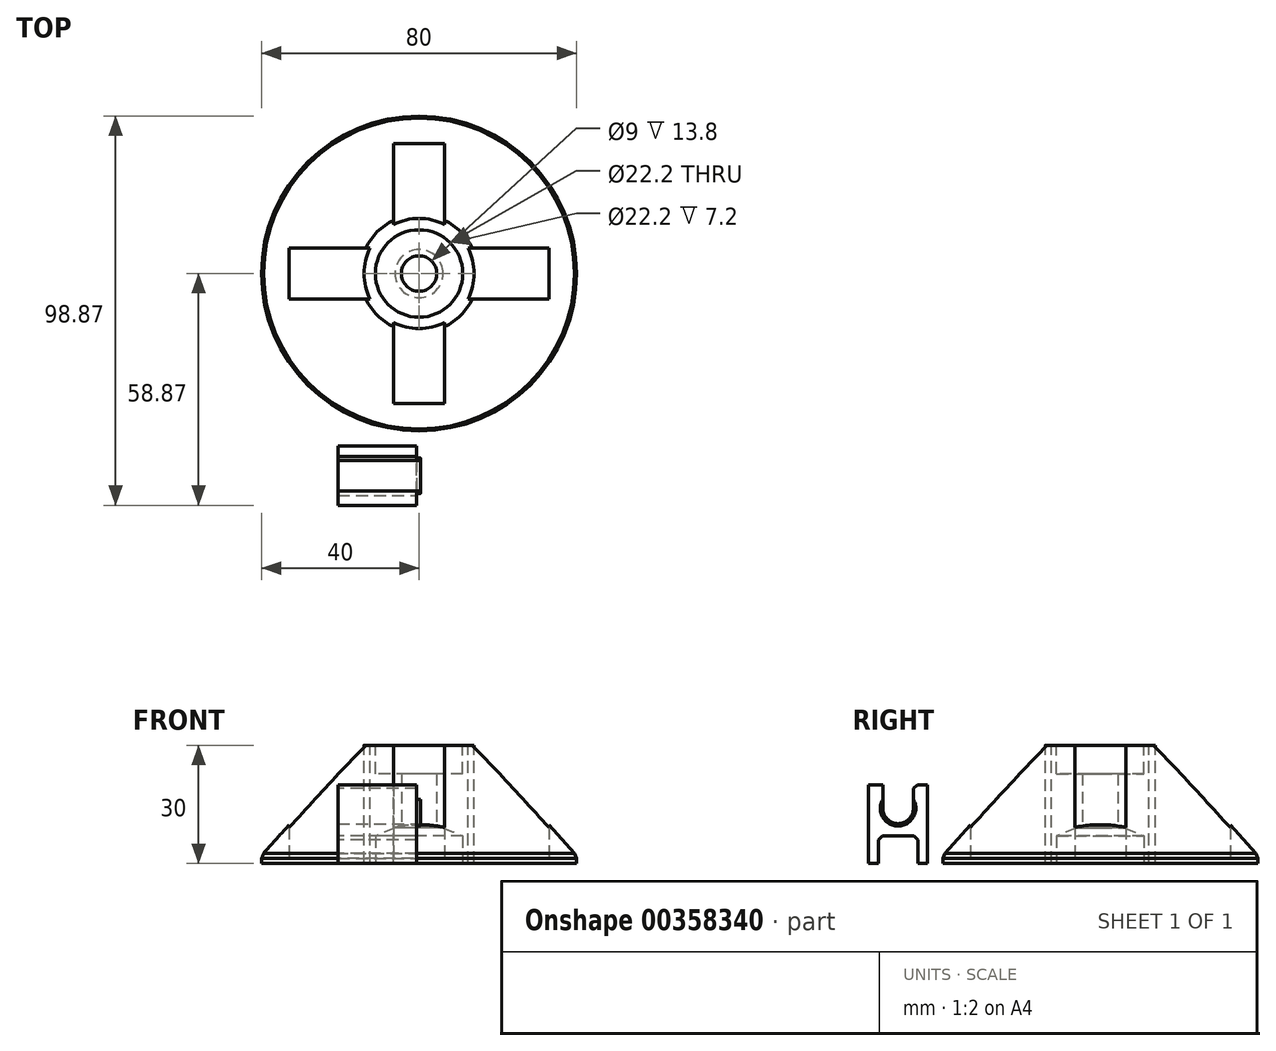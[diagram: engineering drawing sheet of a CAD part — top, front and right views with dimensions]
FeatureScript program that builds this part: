
annotation { "Feature Type Name" : "Feature", "Feature Type Description" : "" }
export const myFeature = defineFeature(function(context is Context, id is Id, definition is map)
    precondition{}
    {
        {
            var Q0;
            Q0=qCreatedBy(makeId("Top.planeOp"),FACE);
            var sketch = newSketch(context, id + "F0", { "sketchPlane" : qUnion([Q0])});
            skCircle(sketch, "E0", {"center": v(0, 0) * mm, "radius": 40 * mm});
            skLineSegment(sketch, "E1.bottom", {"start": v(-6.5, 33) * mm, "end": v(6.5, 33) * mm});
            skLineSegment(sketch, "E1.top", {"start": v(-6.5, 8) * mm, "end": v(6.5, 8) * mm});
            skLineSegment(sketch, "E1.left", {"start": v(-6.5, 33) * mm, "end": v(-6.5, 8) * mm});
            skLineSegment(sketch, "E1.right", {"start": v(6.5, 33) * mm, "end": v(6.5, 8) * mm});
            skPoint(sketch, "E1.middle", {"position": v(0, 20.5) * mm});
            skLineSegment(sketch, "E2", {"start": v(0, 33) * mm, "end": v(0, 40) * mm});
            skCircle(sketch, "E3", {"center": v(0, 0) * mm, "radius": 4.5 * mm});
            skLineSegment(sketch, "E4", {"start": v(0, 20.5) * mm, "end": v(0, 0) * mm});
            skLineSegment(sketch, "E5.bottom", {"start": v(-33, -6.5) * mm, "end": v(-33, 6.5) * mm});
            skLineSegment(sketch, "E5.top", {"start": v(-8, -6.5) * mm, "end": v(-8, 6.5) * mm});
            skLineSegment(sketch, "E5.left", {"start": v(-33, -6.5) * mm, "end": v(-8, -6.5) * mm});
            skLineSegment(sketch, "E5.right", {"start": v(-33, 6.5) * mm, "end": v(-8, 6.5) * mm});
            skPoint(sketch, "E5.middle", {"position": v(-20.5, 0) * mm});
            skLineSegment(sketch, "E6", {"start": v(-20.5, 0) * mm, "end": v(0, 0) * mm});
            skLineSegment(sketch, "E7.bottom", {"start": v(33, 6.5) * mm, "end": v(33, -6.5) * mm});
            skLineSegment(sketch, "E7.top", {"start": v(8, 6.5) * mm, "end": v(8, -6.5) * mm});
            skLineSegment(sketch, "E7.left", {"start": v(33, 6.5) * mm, "end": v(8, 6.5) * mm});
            skLineSegment(sketch, "E7.right", {"start": v(33, -6.5) * mm, "end": v(8, -6.5) * mm});
            skPoint(sketch, "E7.middle", {"position": v(20.5, 0) * mm});
            skLineSegment(sketch, "E8", {"start": v(20.5, 0) * mm, "end": v(0, 0) * mm});
            skLineSegment(sketch, "E9.bottom", {"start": v(6.5, -33) * mm, "end": v(-6.5, -33) * mm});
            skLineSegment(sketch, "E9.top", {"start": v(6.5, -8) * mm, "end": v(-6.5, -8) * mm});
            skLineSegment(sketch, "E9.left", {"start": v(6.5, -33) * mm, "end": v(6.5, -8) * mm});
            skLineSegment(sketch, "E9.right", {"start": v(-6.5, -33) * mm, "end": v(-6.5, -8) * mm});
            skPoint(sketch, "E9.middle", {"position": v(0, -20.5) * mm});
            skLineSegment(sketch, "E10", {"start": v(0, -20.5) * mm, "end": v(0, 0) * mm});
            skSolve(sketch);
        }
        {
            var Q0;
            Q0=qCreatedBy(makeId("Top.planeOp"),FACE);
            cPlane(context, id + "F1", {"entities" : qUnion([Q0]), "cplaneType" : CPlaneType.OFFSET, "offset" : 2 * mm, "width" : 150 * mm, "height" : 150 * mm});
        }
        {
            var Q0;
            Q0=qCreatedBy(id+"F1.planeOp",FACE);
            var sketch = newSketch(context, id + "F2", { "sketchPlane" : qUnion([Q0])});
            skCircle(sketch, "E11", {"center": v(0, 0) * mm, "radius": 40 * mm});
            skSolve(sketch);
        }
        {
            var Q0;
            Q0=qCreatedBy(makeId("Top.planeOp"),FACE);
            cPlane(context, id + "F3", {"entities" : qUnion([Q0]), "cplaneType" : CPlaneType.OFFSET, "offset" : 30 * mm, "width" : 150 * mm, "height" : 150 * mm});
        }
        {
            var Q0;
            Q0=qCreatedBy(id+"F3.planeOp",FACE);
            var sketch = newSketch(context, id + "F4", { "sketchPlane" : qUnion([Q0])});
            skCircle(sketch, "E12", {"center": v(0, 0) * mm, "radius": 15 * mm});
            skSolve(sketch);
        }
        {
            var Q0;
            Q0=makeQuery(id+"F2.imprint","IMPRINT",FACE,{"disambiguationData":[TD([[makeQuery(id+"F2.imprint","IMPRINT",EDGE,{"derivedFrom":sQuery(id+"F2.wireOp",EDGE,"E11")}),1.0]])]});
            var Q1;
            Q1=makeQuery(id+"F4.imprint","IMPRINT",FACE,{"disambiguationData":[TD([[makeQuery(id+"F4.imprint","IMPRINT",EDGE,{"derivedFrom":sQuery(id+"F4.wireOp",EDGE,"E12")}),1.0]])]});
            loft(context, id + "F5", {"sheetProfilesArray" : [{ "sheetProfileEntities" : qUnion([Q0]) }, { "sheetProfileEntities" : qUnion([Q1]) }]});
        }
        {
            var Q0;
            Q0=makeQuery(id+"F0.imprint","IMPRINT",FACE,{"disambiguationData":[TD([[makeQuery(id+"F0.imprint","IMPRINT",EDGE,{"derivedFrom":sQuery(id+"F0.wireOp",EDGE,"E0")}),1.0]])]});
            extrude(context, id + "F6", {"entities" : qUnion([Q0]), "operationType" : NewBodyOperationType.ADD, "depth" : 2 * mm});
        }
        {
            var Q0;
            Q0=makeQuery(id+"F6.boolean.opBoolean","SPLIT",FACE,{"disambiguationData":[TD([makeQuery(id+"F6.opExtrude","SWEPT_FACE",FACE,{"disambiguationData":[OSD([sQuery(id+"F0.wireOp",EDGE,"E5.bottom")])]})])],"derivedFrom":makeQuery(id+"F5.opLoft","CAP_FACE",FACE,{"disambiguationData":[OSD([makeQuery(id+"F2.imprint","IMPRINT",FACE,{"disambiguationData":[TD([[makeQuery(id+"F2.imprint","IMPRINT",EDGE,{"derivedFrom":sQuery(id+"F2.wireOp",EDGE,"E11")}),1.0]])]})])],"isStart":true})});
            var Q1;
            Q1=makeQuery(id+"F6.boolean.opBoolean","SPLIT",FACE,{"disambiguationData":[TD([makeQuery(id+"F6.opExtrude","SWEPT_FACE",FACE,{"disambiguationData":[OSD([sQuery(id+"F0.wireOp",EDGE,"E9.bottom")])]})])],"derivedFrom":makeQuery(id+"F5.opLoft","CAP_FACE",FACE,{"disambiguationData":[OSD([makeQuery(id+"F2.imprint","IMPRINT",FACE,{"disambiguationData":[TD([[makeQuery(id+"F2.imprint","IMPRINT",EDGE,{"derivedFrom":sQuery(id+"F2.wireOp",EDGE,"E11")}),1.0]])]})])],"isStart":true})});
            var Q2;
            Q2=makeQuery(id+"F6.boolean.opBoolean","SPLIT",FACE,{"disambiguationData":[TD([makeQuery(id+"F6.opExtrude","SWEPT_FACE",FACE,{"disambiguationData":[OSD([sQuery(id+"F0.wireOp",EDGE,"E7.bottom")])]})])],"derivedFrom":makeQuery(id+"F5.opLoft","CAP_FACE",FACE,{"disambiguationData":[OSD([makeQuery(id+"F2.imprint","IMPRINT",FACE,{"disambiguationData":[TD([[makeQuery(id+"F2.imprint","IMPRINT",EDGE,{"derivedFrom":sQuery(id+"F2.wireOp",EDGE,"E11")}),1.0]])]})])],"isStart":true})});
            var Q3;
            Q3=makeQuery(id+"F6.boolean.opBoolean","SPLIT",FACE,{"disambiguationData":[TD([makeQuery(id+"F6.opExtrude","SWEPT_FACE",FACE,{"disambiguationData":[OSD([sQuery(id+"F0.wireOp",EDGE,"E1.bottom")])]})])],"derivedFrom":makeQuery(id+"F5.opLoft","CAP_FACE",FACE,{"disambiguationData":[OSD([makeQuery(id+"F2.imprint","IMPRINT",FACE,{"disambiguationData":[TD([[makeQuery(id+"F2.imprint","IMPRINT",EDGE,{"derivedFrom":sQuery(id+"F2.wireOp",EDGE,"E11")}),1.0]])]})])],"isStart":true})});
            var Q4;
            Q4=makeQuery(id+"F6.boolean.opBoolean","SPLIT",FACE,{"disambiguationData":[TD([makeQuery(id+"F6.opExtrude","SWEPT_FACE",FACE,{"disambiguationData":[OSD([sQuery(id+"F0.wireOp",EDGE,"E3")])]})])],"derivedFrom":makeQuery(id+"F5.opLoft","CAP_FACE",FACE,{"disambiguationData":[OSD([makeQuery(id+"F2.imprint","IMPRINT",FACE,{"disambiguationData":[TD([[makeQuery(id+"F2.imprint","IMPRINT",EDGE,{"derivedFrom":sQuery(id+"F2.wireOp",EDGE,"E11")}),1.0]])]})])],"isStart":true})});
            extrude(context, id + "F7", {"entities" : qUnion([Q0, Q1, Q2, Q3, Q4]), "operationType" : NewBodyOperationType.REMOVE, "oppositeDirection" : true, "depth" : 80 * mm});
        }
        {
            var Q0;
            Q0=makeQuery(id+"F6.boolean.opBoolean","MERGE",EDGE,{"derivedFrom":[makeQuery(id+"F5.opLoft","MID_CAP_EDGE",EDGE,{"disambiguationData":[OSD([sQuery(id+"F2.wireOp",EDGE,"E11")])],"capPos":0.0}),makeQuery(id+"F6.opExtrude","CAP_EDGE",EDGE,{"disambiguationData":[OSD([sQuery(id+"F0.wireOp",EDGE,"E0")])],"isStart":false})]});
            chamfer(context, id + "F8", {"entities" : qUnion([Q0]), "width" : 2 * mm, "tangentPropagation" : true});
        }
        {
            var Q0;
            Q0=qCreatedBy(makeId("Top.planeOp"),FACE);
            var sketch = newSketch(context, id + "F9", { "sketchPlane" : qUnion([Q0])});
            skLineSegment(sketch, "E13.bottom", {"start": v(-0.6, -43.87) * mm, "end": v(-20.6, -43.87) * mm});
            skLineSegment(sketch, "E13.top", {"start": v(-0.6, -58.87) * mm, "end": v(-20.6, -58.87) * mm});
            skLineSegment(sketch, "E13.left", {"start": v(-0.6, -43.87) * mm, "end": v(-0.6, -58.87) * mm});
            skLineSegment(sketch, "E13.right", {"start": v(-20.6, -43.87) * mm, "end": v(-20.6, -58.87) * mm});
            skPoint(sketch, "E13.middle", {"position": v(-10.6, -51.37) * mm});
            skSolve(sketch);
        }
        {
            var Q0;
            Q0 = qSketchRegion(id + "F9", true);
            var Q1;
            Q1=makeQuery(id+"F9.imprint","IMPRINT",FACE,{"disambiguationData":[TD([[makeQuery(id+"F9.imprint","IMPRINT",EDGE,{"derivedFrom":sQuery(id+"F9.wireOp",EDGE,"E13.bottom")}),1.0]])]});
            extrude(context, id + "F10", {"entities" : qUnion([Q0, Q1]), "depth" : 20 * mm});
        }
        {
            var Q0;
            Q0=makeQuery(id+"F10.opExtrude","SWEPT_FACE",FACE,{"disambiguationData":[OSD([sQuery(id+"F9.wireOp",EDGE,"E13.left")])]});
            var sketch = newSketch(context, id + "F11", { "sketchPlane" : qUnion([Q0])});
            skLineSegment(sketch, "E14", {"start": v(-51.37, 20) * mm, "end": v(-51.37, 14) * mm});
            skCircle(sketch, "E15", {"center": v(-51.37, 14) * mm, "radius": 3.9 * mm});
            skLineSegment(sketch, "E16", {"start": v(-55.27, 14) * mm, "end": v(-55.27, 20) * mm});
            skLineSegment(sketch, "E17", {"start": v(-47.47, 14) * mm, "end": v(-47.47, 20) * mm});
            skLineSegment(sketch, "E18", {"start": v(-51.37, 0) * mm, "end": v(-51.37, 7) * mm});
            skLineSegment(sketch, "E19", {"start": v(-51.37, 7) * mm, "end": v(-46.37, 7) * mm});
            skLineSegment(sketch, "E20", {"start": v(-51.37, 7) * mm, "end": v(-56.37, 7) * mm});
            skCircle(sketch, "E21", {"center": v(-51.37, 14) * mm, "radius": 4.5 * mm});
            skLineSegment(sketch, "E22", {"start": v(-56.37, 7) * mm, "end": v(-56.37, 0) * mm});
            skLineSegment(sketch, "E23", {"start": v(-46.37, 7) * mm, "end": v(-46.37, 0) * mm});
            skSolve(sketch);
        }
        {
            var Q0;
            {var subQ0=sQuery(id+"F11.wireOp",EDGE,"E14");var subQ1=makeQuery(id+"F10.opExtrude","CAP_EDGE",EDGE,{"disambiguationData":[OSD([sQuery(id+"F9.wireOp",EDGE,"E13.left")])],"isStart":false});var subQ2=makeQuery(id+"F11.imprint","INTERSECT",VERTEX,{"derivedFrom":[subQ1,subQ0]});Q0=makeQuery(id+"F11.imprint","IMPRINT",FACE,{"disambiguationData":[TD([[makeQuery(id+"F11.imprint","IMPRINT",EDGE,{"disambiguationData":[TD([[subQ2,-1.0]])],"derivedFrom":subQ0}),-1.0]])]});}
            var Q1;
            {var subQ0=sQuery(id+"F11.wireOp",EDGE,"E14");var subQ1=makeQuery(id+"F10.opExtrude","CAP_EDGE",EDGE,{"disambiguationData":[OSD([sQuery(id+"F9.wireOp",EDGE,"E13.left")])],"isStart":false});var subQ2=makeQuery(id+"F11.imprint","INTERSECT",VERTEX,{"derivedFrom":[subQ1,subQ0]});Q1=makeQuery(id+"F11.imprint","IMPRINT",FACE,{"disambiguationData":[TD([[makeQuery(id+"F11.imprint","IMPRINT",EDGE,{"disambiguationData":[TD([[subQ2,-1.0]])],"derivedFrom":subQ0}),1.0]])]});}
            var Q2;
            {var subQ0=sQuery(id+"F11.wireOp",EDGE,"E15");var subQ1=sQuery(id+"F11.wireOp",EDGE,"E14");var subQ2=makeQuery(id+"F11.imprint","INTERSECT",VERTEX,{"derivedFrom":[subQ1,subQ0]});Q2=makeQuery(id+"F11.imprint","IMPRINT",FACE,{"disambiguationData":[TD([[makeQuery(id+"F11.imprint","IMPRINT",EDGE,{"disambiguationData":[TD([[subQ2,1.0]])],"derivedFrom":subQ1}),1.0]])]});}
            var Q3;
            {var subQ0=sQuery(id+"F11.wireOp",EDGE,"E15");var subQ1=sQuery(id+"F11.wireOp",EDGE,"E14");var subQ2=makeQuery(id+"F11.imprint","INTERSECT",VERTEX,{"derivedFrom":[subQ1,subQ0]});Q3=makeQuery(id+"F11.imprint","IMPRINT",FACE,{"disambiguationData":[TD([[makeQuery(id+"F11.imprint","IMPRINT",EDGE,{"disambiguationData":[TD([[subQ2,1.0]])],"derivedFrom":subQ1}),-1.0]])]});}
            var Q4;
            {var subQ0=sQuery(id+"F11.wireOp",EDGE,"E15");var subQ1=makeQuery(id+"F11.imprint","INTERSECT",VERTEX,{"derivedFrom":[subQ0,sQuery(id+"F11.wireOp",EDGE,"E17")]});Q4=makeQuery(id+"F11.imprint","IMPRINT",FACE,{"disambiguationData":[TD([[makeQuery(id+"F11.imprint","IMPRINT",EDGE,{"disambiguationData":[TD([[subQ1,-1.0]])],"derivedFrom":subQ0}),1.0]])]});}
            var Q5;
            {var subQ0=sQuery(id+"F11.wireOp",EDGE,"E18");Q5=makeQuery(id+"F11.imprint","IMPRINT",FACE,{"disambiguationData":[TD([[makeQuery(id+"F11.imprint","IMPRINT",EDGE,{"derivedFrom":subQ0}),1.0]])]});}
            var Q6;
            {var subQ0=sQuery(id+"F11.wireOp",EDGE,"E18");Q6=makeQuery(id+"F11.imprint","IMPRINT",FACE,{"disambiguationData":[TD([[makeQuery(id+"F11.imprint","IMPRINT",EDGE,{"derivedFrom":subQ0}),-1.0]])]});}
            extrude(context, id + "F12", {"entities" : qUnion([Q0, Q1, Q2, Q3, Q4, Q5, Q6]), "operationType" : NewBodyOperationType.REMOVE, "oppositeDirection" : true, "depth" : 20 * mm});
        }
        {
            var Q0;
            {var subQ0=sQuery(id+"F11.wireOp",EDGE,"E16");var subQ1=sQuery(id+"F11.wireOp",EDGE,"E15");var subQ2=makeQuery(id+"F11.imprint","INTERSECT",VERTEX,{"derivedFrom":[subQ1,subQ0]});Q0=makeQuery(id+"F11.imprint","IMPRINT",FACE,{"disambiguationData":[TD([[makeQuery(id+"F11.imprint","IMPRINT",EDGE,{"disambiguationData":[TD([[subQ2,-1.0]])],"derivedFrom":subQ1}),-1.0]])]});}
            extrude(context, id + "F13", {"entities" : qUnion([Q0]), "operationType" : NewBodyOperationType.ADD, "depth" : 1 * mm});
        }
        {
            var Q0;
            Q0=makeQuery(id+"F12.boolean.opBoolean","COPY",EDGE,{"derivedFrom":makeQuery(id+"F12.opExtrude","SWEPT_EDGE",EDGE,{"disambiguationData":[OSD([sQuery(id+"F11.wireOp",EDGE,"E20"),sQuery(id+"F11.wireOp",EDGE,"E22")])]})});
            var Q1;
            Q1=makeQuery(id+"F12.boolean.opBoolean","COPY",EDGE,{"derivedFrom":makeQuery(id+"F12.opExtrude","SWEPT_EDGE",EDGE,{"disambiguationData":[OSD([sQuery(id+"F11.wireOp",EDGE,"E19"),sQuery(id+"F11.wireOp",EDGE,"E23")])]})});
            var Q2;
            Q2=makeQuery(id+"F13.opExtrude","CAP_EDGE",EDGE,{"disambiguationData":[OSD([sQuery(id+"F11.wireOp",EDGE,"E21")])],"isStart":true});
            var Q3;
            Q3=makeQuery(id+"F12.boolean.opBoolean","COPY",EDGE,{"derivedFrom":makeQuery(id+"F12.opExtrude","SWEPT_EDGE",EDGE,{"disambiguationData":[OSD([sQuery(id+"F9.wireOp",EDGE,"E13.left"),sQuery(id+"F11.wireOp",EDGE,"E16")])]})});
            var Q4;
            Q4=makeQuery(id+"F12.boolean.opBoolean","COPY",EDGE,{"derivedFrom":makeQuery(id+"F12.opExtrude","SWEPT_EDGE",EDGE,{"disambiguationData":[OSD([sQuery(id+"F9.wireOp",EDGE,"E13.left"),sQuery(id+"F11.wireOp",EDGE,"E17")])]})});
            chamfer(context, id + "F14", {"entities" : qUnion([Q0, Q1, Q2, Q3, Q4]), "width" : 1 * mm, "tangentPropagation" : true});
        }
        {
            var Q0;
            Q0=makeQuery(id+"F5.opLoft","CAP_FACE",FACE,{"disambiguationData":[OSD([makeQuery(id+"F4.imprint","IMPRINT",FACE,{"disambiguationData":[TD([[makeQuery(id+"F4.imprint","IMPRINT",EDGE,{"derivedFrom":sQuery(id+"F4.wireOp",EDGE,"E12")}),1.0]])]})])],"isStart":true});
            var sketch = newSketch(context, id + "F15", { "sketchPlane" : qUnion([Q0])});
            skCircle(sketch, "E24", {"center": v(0, 0) * mm, "radius": 14 * mm});
            skSolve(sketch);
        }
        {
            var Q0;
            {var subQ1=makeQuery(id+"F5.opLoft","CAP_FACE",FACE,{"disambiguationData":[OSD([makeQuery(id+"F4.imprint","IMPRINT",FACE,{"disambiguationData":[TD([[makeQuery(id+"F4.imprint","IMPRINT",EDGE,{"derivedFrom":sQuery(id+"F4.wireOp",EDGE,"E12")}),1.0]])]})])],"isStart":true});var subQ6=makeQuery(id+"F7.boolean.opBoolean","INTERSECT",EDGE,{"derivedFrom":[subQ1,makeQuery(id+"F7.opExtrude","SWEPT_FACE",FACE,{"disambiguationData":[OSD([sQuery(id+"F0.wireOp",EDGE,"E1.top")])]})]});Q0=makeQuery(id+"F15.imprint","IMPRINT",FACE,{"disambiguationData":[TD([[makeQuery(id+"F15.imprint","IMPRINT",EDGE,{"derivedFrom":subQ6}),-1.0]])]});}
            var Q1;
            {var subQ1=makeQuery(id+"F5.opLoft","CAP_FACE",FACE,{"disambiguationData":[OSD([makeQuery(id+"F4.imprint","IMPRINT",FACE,{"disambiguationData":[TD([[makeQuery(id+"F4.imprint","IMPRINT",EDGE,{"derivedFrom":sQuery(id+"F4.wireOp",EDGE,"E12")}),1.0]])]})])],"isStart":true});var subQ6=makeQuery(id+"F7.boolean.opBoolean","INTERSECT",EDGE,{"derivedFrom":[subQ1,makeQuery(id+"F7.opExtrude","SWEPT_FACE",FACE,{"disambiguationData":[OSD([sQuery(id+"F0.wireOp",EDGE,"E5.top")])]})]});Q1=makeQuery(id+"F15.imprint","IMPRINT",FACE,{"disambiguationData":[TD([[makeQuery(id+"F15.imprint","IMPRINT",EDGE,{"derivedFrom":subQ6}),-1.0]])]});}
            var Q2;
            {var subQ1=makeQuery(id+"F5.opLoft","CAP_FACE",FACE,{"disambiguationData":[OSD([makeQuery(id+"F4.imprint","IMPRINT",FACE,{"disambiguationData":[TD([[makeQuery(id+"F4.imprint","IMPRINT",EDGE,{"derivedFrom":sQuery(id+"F4.wireOp",EDGE,"E12")}),1.0]])]})])],"isStart":true});var subQ6=makeQuery(id+"F7.boolean.opBoolean","INTERSECT",EDGE,{"derivedFrom":[subQ1,makeQuery(id+"F7.opExtrude","SWEPT_FACE",FACE,{"disambiguationData":[OSD([sQuery(id+"F0.wireOp",EDGE,"E9.top")])]})]});Q2=makeQuery(id+"F15.imprint","IMPRINT",FACE,{"disambiguationData":[TD([[makeQuery(id+"F15.imprint","IMPRINT",EDGE,{"derivedFrom":subQ6}),-1.0]])]});}
            var Q3;
            {var subQ1=makeQuery(id+"F5.opLoft","CAP_FACE",FACE,{"disambiguationData":[OSD([makeQuery(id+"F4.imprint","IMPRINT",FACE,{"disambiguationData":[TD([[makeQuery(id+"F4.imprint","IMPRINT",EDGE,{"derivedFrom":sQuery(id+"F4.wireOp",EDGE,"E12")}),1.0]])]})])],"isStart":true});var subQ6=makeQuery(id+"F7.boolean.opBoolean","INTERSECT",EDGE,{"derivedFrom":[subQ1,makeQuery(id+"F7.opExtrude","SWEPT_FACE",FACE,{"disambiguationData":[OSD([sQuery(id+"F0.wireOp",EDGE,"E7.top")])]})]});Q3=makeQuery(id+"F15.imprint","IMPRINT",FACE,{"disambiguationData":[TD([[makeQuery(id+"F15.imprint","IMPRINT",EDGE,{"derivedFrom":subQ6}),-1.0]])]});}
            var Q4;
            {var subQ0=makeQuery(id+"F5.opLoft","CAP_FACE",FACE,{"disambiguationData":[OSD([makeQuery(id+"F4.imprint","IMPRINT",FACE,{"disambiguationData":[TD([[makeQuery(id+"F4.imprint","IMPRINT",EDGE,{"derivedFrom":sQuery(id+"F4.wireOp",EDGE,"E12")}),1.0]])]})])],"isStart":true});Q4=makeQuery(id+"F15.imprint","IMPRINT",FACE,{"disambiguationData":[TD([[makeQuery(id+"F15.imprint","IMPRINT",EDGE,{"derivedFrom":makeQuery(id+"F7.boolean.opBoolean","INTERSECT",EDGE,{"derivedFrom":[subQ0,makeQuery(id+"F7.opExtrude","SWEPT_FACE",FACE,{"disambiguationData":[OSD([sQuery(id+"F0.wireOp",EDGE,"E3")])]})]})}),1.0]])]});}
            var Q5;
            Q5=sQuery(id+"F15.wireOp",EDGE,"E24");
            extrude(context, id + "F16", {"entities" : qUnion([Q0, Q1, Q2, Q3, Q4]), "operationType" : NewBodyOperationType.ADD, "surfaceEntities" : qUnion([Q5]), "oppositeDirection" : true, "depth" : 30 * mm});
        }
        {
            var Q0;
            Q0=qCreatedBy(makeId("Top.planeOp"),FACE);
            var sketch = newSketch(context, id + "F17", { "sketchPlane" : qUnion([Q0])});
            skCircle(sketch, "E25", {"center": v(0, 0) * mm, "radius": 11.1 * mm});
            skSolve(sketch);
        }
        {
            var Q0;
            Q0 = qSketchRegion(id + "F17", true);
            extrude(context, id + "F18", {"entities" : qUnion([Q0]), "operationType" : NewBodyOperationType.REMOVE, "depth" : 9 * mm});
        }
        {
            var Q0;
            {var subQ0=makeQuery(id+"F4.imprint","IMPRINT",FACE,{"disambiguationData":[TD([[makeQuery(id+"F4.imprint","IMPRINT",EDGE,{"derivedFrom":sQuery(id+"F4.wireOp",EDGE,"E12")}),1.0]])]});Q0=makeQuery(id+"F16.boolean.opBoolean","MERGE",FACE,{"derivedFrom":[makeQuery(id+"F5.opLoft","CAP_FACE",FACE,{"disambiguationData":[OSD([subQ0])],"isStart":true}),makeQuery(id+"F16.opExtrude","CAP_FACE",FACE,{"disambiguationData":[OSD([sQuery(id+"F0.wireOp",EDGE,"E3"),subQ0,sQuery(id+"F15.wireOp",EDGE,"E24")])],"isStart":true})]});}
            var sketch = newSketch(context, id + "F19", { "sketchPlane" : qUnion([Q0])});
            skCircle(sketch, "E26", {"center": v(0, 0) * mm, "radius": 11.1 * mm});
            skSolve(sketch);
        }
        {
            var Q0;
            Q0=makeQuery(id+"F19.imprint","IMPRINT",FACE,{"disambiguationData":[TD([[makeQuery(id+"F19.imprint","IMPRINT",EDGE,{"derivedFrom":sQuery(id+"F19.wireOp",EDGE,"E26")}),1.0]])]});
            extrude(context, id + "F20", {"entities" : qUnion([Q0]), "operationType" : NewBodyOperationType.REMOVE, "oppositeDirection" : true, "depth" : 7.2 * mm});
        }
        {
            var Q0;
            Q0=makeQuery(id+"F18.boolean.opBoolean","COPY",EDGE,{"derivedFrom":makeQuery(id+"F18.opExtrude","CAP_EDGE",EDGE,{"disambiguationData":[OSD([sQuery(id+"F17.wireOp",EDGE,"E25")])],"isStart":false})});
            chamfer(context, id + "F21", {"entities" : qUnion([Q0]), "chamferType" : ChamferType.TWO_OFFSETS, "width1" : 2 * mm, "oppositeDirection" : false, "width2" : 5 * mm, "tangentPropagation" : true});
        }
    });
